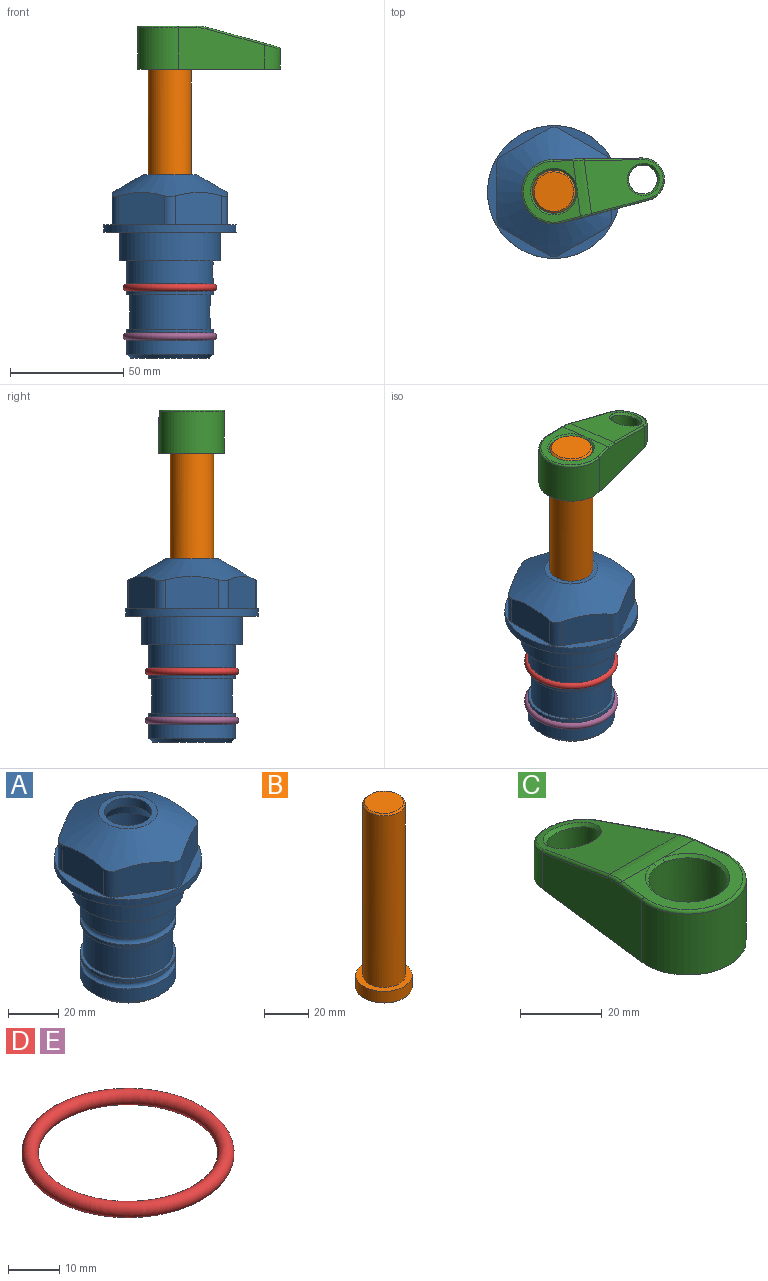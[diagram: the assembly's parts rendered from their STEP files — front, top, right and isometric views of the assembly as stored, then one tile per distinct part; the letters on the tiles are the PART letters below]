
ASSEMBLY  parts=5 mates=4
PART A: 36 faces, bbox 58.7x58.7x81 mm
  f0: cylinder r=17.78mm len=35.56mm, axis (0,0,1), area 1670.8mm2, adj f23,f24,f31
  f1: cylinder r=19.05mm len=38.1mm, axis (0,0,1), area 1191.9mm2, adj f26,f27,f30
  f2: plane 58.66x58.66mm, normal (0,0,-1), area 1150.6mm2, adj f3,f28
  f3: cylinder r=29.33mm len=58.66mm, axis (0,0,-1), area 585.1mm2, adj f2,f4
  f4: plane 58.66x58.66mm, normal (0,0,1), area 475.9mm2, adj f3,f5,f6,f7,f8,f9,f10,f11
  f5: plane 20.32x14.34mm, normal (-0.5,0.87,0), area 324.4mm2, adj f4,f15,f16,f17
  f6: plane 20.32x14.34mm, normal (0.5,0.87,0), area 324.4mm2, adj f4,f14,f15,f17
  f7: plane 23.48x14.34mm, normal (1,0,0), area 324.4mm2, adj f4,f13,f14,f17
  f8: plane 20.32x14.34mm, normal (0.5,-0.87,0), area 324.4mm2, adj f4,f12,f13,f17
  f9: plane 20.32x14.34mm, normal (-0.5,-0.87,0), area 324.4mm2, adj f4,f11,f12,f17
  f10: plane 23.48x14.34mm, normal (-1,0,0), area 324.4mm2, adj f4,f11,f16,f17
  f11: cylinder r=5.08mm len=12.85mm, axis (0,0,-1), area 67.2mm2, adj f4,f9,f10,f17
  f12: cylinder r=5.08mm len=12.85mm, axis (0,0,-1), area 67.2mm2, adj f4,f8,f9,f17
  f13: cylinder r=5.08mm len=12.85mm, axis (0,0,-1), area 67.2mm2, adj f4,f7,f8,f17
  f14: cylinder r=5.08mm len=12.85mm, axis (0,0,-1), area 67.2mm2, adj f4,f6,f7,f17
  f15: cylinder r=5.08mm len=12.85mm, axis (0,0,-1), area 67.2mm2, adj f4,f5,f6,f17
  f16: cylinder r=5.08mm len=12.85mm, axis (0,0,-1), area 67.2mm2, adj f4,f5,f10,f17
  f17: cone r=11.73mm half-angle=60deg, axis (0,0,-1), area 2071.8mm2, adj f5,f6,f7,f8,f9,f10,f11,f12
  f18: plane 23.46x23.46mm, normal (0,0,1), area 147.4mm2, adj f17,f35
  f19: plane 34.93x34.93mm, normal (0,0,-1), area 958mm2, adj f29
  f20: cylinder r=19.05mm len=38.1mm, axis (0,0,1), area 760.1mm2, adj f21,f29
  f21: torus R=19.05mm, axis (0,0,1), area 565.3mm2, adj f20,f22
  f22: cylinder r=19.05mm len=38.1mm, axis (0,0,1), area 190mm2, adj f21,f23
  f23: plane 38.1x38.1mm, normal (0,0,1), area 146.9mm2, adj f0,f22
  f24: plane 38.1x38.1mm, normal (0,0,-1), area 146.9mm2, adj f0,f25
  f25: cylinder r=19.05mm len=38.1mm, axis (0,0,1), area 190mm2, adj f24,f26
  f26: torus R=19.05mm, axis (0,0,1), area 565.3mm2, adj f1,f25
  f27: plane 44.45x44.45mm, normal (0,0,-1), area 411.7mm2, adj f1,f28
  f28: cylinder r=22.23mm len=44.45mm, axis (0,0,1), area 1773.5mm2, adj f2,f27
  f29: cone r=19.05mm half-angle=45deg, axis (0,0,1), area 257.5mm2, adj f19,f20
  f30: cylinder r=3.17mm len=6.75mm, axis (-1,0,0), area 128mm2, adj f1,f33
  f31: cylinder r=3.17mm len=6.35mm, axis (-1,0,0), area 102.5mm2, adj f0,f33
  f32: plane 25.4x25.4mm, normal (0,0,1), area 506.7mm2, adj f33
  f33: cylinder r=12.7mm len=66.42mm, axis (0,0,-1), area 5236.2mm2, adj f30,f31,f32,f34
  f34: cone r=9.53mm half-angle=30deg, axis (0,0,-1), area 443.4mm2, adj f33,f35
  f35: cylinder r=9.53mm len=19.05mm, axis (0,0,-1), area 240.9mm2, adj f18,f34
PART B: 6 faces, bbox 25.4x25.4x101.6 mm
  f0: plane 17.46x17.46mm, normal (0,0,1), area 239.5mm2, adj f5
  f1: plane 25.4x25.4mm, normal (0,0,-1), area 506.7mm2, adj f2
  f2: cylinder r=12.7mm len=25.4mm, axis (0,0,1), area 506.7mm2, adj f1,f3
  f3: plane 25.4x25.4mm, normal (0,0,1), area 221.7mm2, adj f2,f4
  f4: cylinder r=9.53mm len=94.46mm, axis (0,0,1), area 5653mm2, adj f3,f5
  f5: cone r=8.73mm half-angle=45deg, axis (0,0,-1), area 64.4mm2, adj f0,f4
PART C: 31 faces, bbox 31.7x65.5x19.8 mm
  f0: plane 39.12x18.26mm, normal (0.99,0.12,0), area 612.2mm2, adj f1,f4,f7,f11,f13,f15
  f1: cylinder r=9.53mm len=18.91mm, axis (0,0,-1), area 296.1mm2, adj f0,f2,f7,f17
  f2: plane 39.12x18.26mm, normal (-0.99,0.12,0), area 612.2mm2, adj f1,f4,f7,f12,f14,f16
  f3: cylinder r=6.35mm len=12.7mm, axis (0,0,-1), area 362.4mm2, adj f7,f18
  f4: cylinder r=14.29mm len=28.58mm, axis (0,0,-1), area 882.2mm2, adj f0,f2,f7,f10
  f5: cylinder r=9.53mm len=19.05mm, axis (0,0,-1), area 1092.6mm2, adj f7,f19,f20
  f6: plane 26.99x23.69mm, normal (0,0,1), area 216.2mm2, adj f9,f10,f11,f12,f19
  f7: plane 63.5x28.58mm, normal (0,0,-1), area 661.8mm2, adj f0,f1,f2,f3,f4,f5,f22,f23
  f8: plane 33.52x23.6mm, normal (0,0.26,0.97), area 486mm2, adj f9,f15,f16,f17,f18
  f9: cylinder r=19.05mm len=24.72mm, axis (1,0,0), area 120.4mm2, adj f6,f8,f13,f14,f20
  f10: torus R=13.49mm, axis (0,0,1), area 59mm2, adj f4,f6,f11,f12
  f11: cylinder r=0.79mm len=8.67mm, axis (0.12,-0.99,0), area 10.8mm2, adj f0,f6,f10,f13
  f12: cylinder r=0.79mm len=8.67mm, axis (0.12,0.99,0), area 10.8mm2, adj f2,f6,f10,f14
  f13: bspline ~4.95x1.42mm, area 6.1mm2, adj f0,f9,f11,f15
  f14: bspline ~4.95x1.42mm, area 6.1mm2, adj f2,f9,f12,f16
  f15: cylinder r=0.79mm len=25.95mm, axis (0.12,-0.96,0.26), area 32.9mm2, adj f0,f8,f13,f17
  f16: cylinder r=0.79mm len=25.95mm, axis (0.12,0.96,-0.26), area 32.9mm2, adj f2,f8,f14,f17
  f17: bspline ~18.91x8.38mm, area 30mm2, adj f1,f8,f15,f16
  f18: bspline ~14.29x14.29mm, area 48.3mm2, adj f3,f8
  f19: cone r=9.53mm half-angle=45deg, axis (0,0,1), area 66.5mm2, adj f5,f6,f20
  f20: bspline ~3.22x0.96mm, area 3.5mm2, adj f5,f9,f19
  f21: plane 2.75x2.72mm, normal (0,0,-1), area 2.9mm2, adj f23,f25,f28
  f22: plane 23.05x15.88mm, normal (-0.99,-0.12,0), area 323.6mm2, adj f7,f25,f26,f27,f28,f29
  f23: plane 23.05x15.88mm, normal (0.99,-0.12,0), area 323.6mm2, adj f7,f21,f25,f27,f28,f30
  f24: cylinder r=9.53mm len=10.69mm, axis (0,0,-1), area 114.7mm2, adj f7,f27,f29,f30
  f25: cylinder r=12.7mm len=20.59mm, axis (0,0,-1), area 381.1mm2, adj f7,f21,f22,f23,f26,f28
  f26: plane 2.75x2.72mm, normal (0,0,-1), area 2.9mm2, adj f22,f25,f28
  f27: plane 19.72x18.37mm, normal (0,-0.26,-0.97), area 291.8mm2, adj f22,f23,f24,f28,f29,f30
  f28: cylinder r=15.88mm len=19.92mm, axis (1,0,0), area 54.8mm2, adj f21,f22,f23,f25,f26,f27
  f29: cylinder r=1.59mm len=11mm, axis (0,0,-1), area 34.7mm2, adj f7,f22,f24,f27
  f30: cylinder r=1.59mm len=11mm, axis (0,0,-1), area 34.7mm2, adj f7,f23,f24,f27
PART D: 1 faces, bbox 44.7x44.7x3.2 mm
  f0: torus R=19.05mm, axis (0,0,1), area 1193.9mm2
PART E: same geometry as D
PLACE A at identity fixed
PLACE B rot(axis=(0,0,-1),82.2deg) t=(0,0,27.55)mm
PLACE C rot(axis=(0,0,-1),82.2deg) t=(0,0,27.55)mm
PLACE D at identity
PLACE E t=(0,0,-21.59)mm
MATE cylindrical B.f2 <-> A.f0  axis (0,0,-1) through (0,0,-10.55)mm
MATE fastened C.f4 <-> B.f2  axis (0,0,1) through (0,0,91.05)mm
MATE fastened D.f0 <-> A.f0  axis (0,0,1) through (0,0,-24.51)mm
MATE fastened E.f0 <-> A.f0  axis (0,0,1) through (0,0,-46.1)mm
